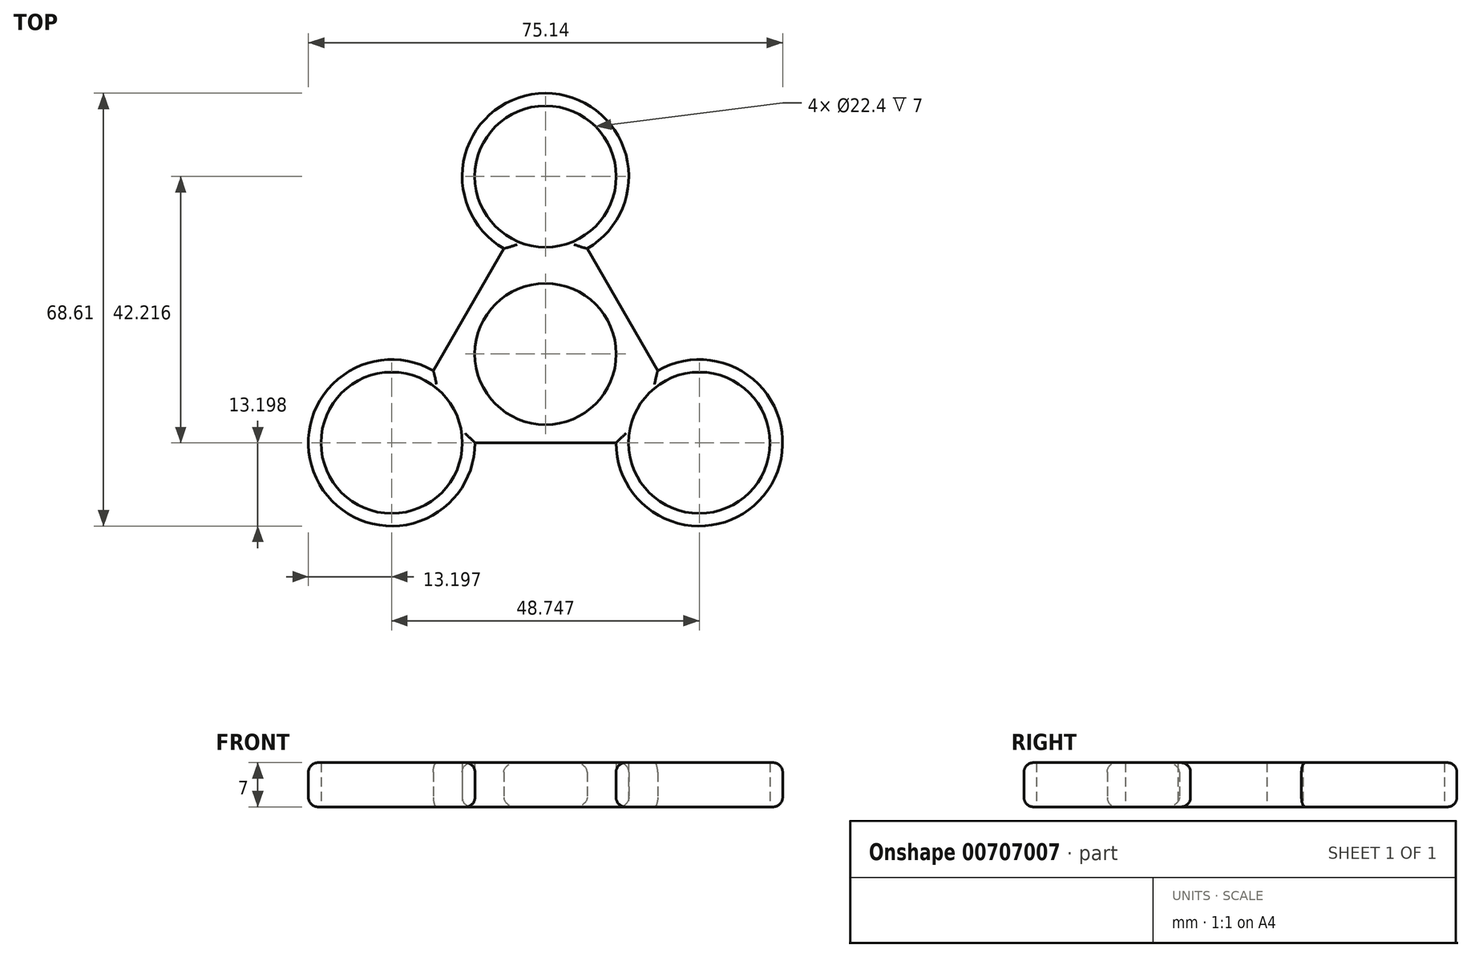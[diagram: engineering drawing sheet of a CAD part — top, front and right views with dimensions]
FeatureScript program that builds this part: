
annotation { "Feature Type Name" : "Feature", "Feature Type Description" : "" }
export const myFeature = defineFeature(function(context is Context, id is Id, definition is map)
    precondition{}
    {
        {
            var Q0;
            Q0=qCreatedBy(makeId("Top.planeOp"),FACE);
            var sketch = newSketch(context, id + "F0", { "sketchPlane" : qUnion([Q0])});
            skCircle(sketch, "E0", {"center": v(0, 0) * mm, "radius": 11.2 * mm});
            skCircle(sketch, "E1", {"center": v(0, 28.14) * mm, "radius": 11.2 * mm});
            skArc(sketch, "E2", {"start": v(6.6, 16.71) * mm, "mid": v(0, 41.34) * mm, "end": v(-6.6, 16.71) * mm});
            skArc(sketch, "E3.1.0", {"start": v(-17.77, -2.64) * mm, "mid": v(-35.8, -20.67) * mm, "end": v(-11.17, -14.07) * mm});
            skCircle(sketch, "E3.1.1", {"center": v(-24.37, -14.07) * mm, "radius": 11.2 * mm});
            skArc(sketch, "E3.2.0", {"start": v(11.17, -14.07) * mm, "mid": v(35.8, -20.67) * mm, "end": v(17.77, -2.64) * mm});
            skCircle(sketch, "E3.2.1", {"center": v(24.37, -14.07) * mm, "radius": 11.2 * mm});
            skLineSegment(sketch, "E4", {"start": v(-11.17, -14.07) * mm, "end": v(11.17, -14.07) * mm});
            skLineSegment(sketch, "E5.1.0", {"start": v(17.77, -2.64) * mm, "end": v(6.6, 16.71) * mm});
            skLineSegment(sketch, "E5.2.0", {"start": v(-6.6, 16.71) * mm, "end": v(-17.77, -2.64) * mm});
            skSolve(sketch);
        }
        {
            var Q0;
            Q0=makeQuery(id+"F0.imprint","IMPRINT",FACE,{"disambiguationData":[TD([[makeQuery(id+"F0.imprint","IMPRINT",EDGE,{"derivedFrom":sQuery(id+"F0.wireOp",EDGE,"E0")}),-1.0]])]});
            extrude(context, id + "F1", {"entities" : qUnion([Q0]), "depth" : 7 * mm, "offsetDistance" : 25 * mm});
        }
        {
            var Q0;
            Q0=makeQuery(id+"F1.opExtrude","CAP_EDGE",EDGE,{"disambiguationData":[OSD([sQuery(id+"F0.wireOp",EDGE,"E4")])],"isStart":false});
            var Q1;
            Q1=makeQuery(id+"F1.opExtrude","CAP_EDGE",EDGE,{"disambiguationData":[OSD([sQuery(id+"F0.wireOp",EDGE,"E4")])],"isStart":true});
            var Q2;
            Q2=makeQuery(id+"F1.opExtrude","CAP_EDGE",EDGE,{"disambiguationData":[OSD([sQuery(id+"F0.wireOp",EDGE,"E3.1.0")])],"isStart":false});
            var Q3;
            Q3=makeQuery(id+"F1.opExtrude","CAP_EDGE",EDGE,{"disambiguationData":[OSD([sQuery(id+"F0.wireOp",EDGE,"E5.2.0")])],"isStart":false});
            var Q4;
            Q4=makeQuery(id+"F1.opExtrude","CAP_EDGE",EDGE,{"disambiguationData":[OSD([sQuery(id+"F0.wireOp",EDGE,"E2")])],"isStart":false});
            var Q5;
            Q5=makeQuery(id+"F1.opExtrude","CAP_EDGE",EDGE,{"disambiguationData":[OSD([sQuery(id+"F0.wireOp",EDGE,"E5.1.0")])],"isStart":false});
            var Q6;
            Q6=makeQuery(id+"F1.opExtrude","CAP_EDGE",EDGE,{"disambiguationData":[OSD([sQuery(id+"F0.wireOp",EDGE,"E3.2.0")])],"isStart":false});
            fillet(context, id + "F2", {"entities" : qUnion([Q0, Q1, Q2, Q3, Q4, Q5, Q6]), "radius" : 1.5 * mm, "tangentPropagation" : true, "allowEdgeOverflow" : false});
        }
        {
            var Q0;
            Q0=makeQuery(id+"F1.opExtrude","CAP_EDGE",EDGE,{"disambiguationData":[OSD([sQuery(id+"F0.wireOp",EDGE,"E3.1.0")])],"isStart":true});
            var Q1;
            Q1=makeQuery(id+"F1.opExtrude","CAP_EDGE",EDGE,{"disambiguationData":[OSD([sQuery(id+"F0.wireOp",EDGE,"E5.2.0")])],"isStart":true});
            var Q2;
            Q2=makeQuery(id+"F1.opExtrude","CAP_EDGE",EDGE,{"disambiguationData":[OSD([sQuery(id+"F0.wireOp",EDGE,"E2")])],"isStart":true});
            var Q3;
            Q3=makeQuery(id+"F1.opExtrude","CAP_EDGE",EDGE,{"disambiguationData":[OSD([sQuery(id+"F0.wireOp",EDGE,"E5.1.0")])],"isStart":true});
            var Q4;
            Q4=makeQuery(id+"F1.opExtrude","CAP_EDGE",EDGE,{"disambiguationData":[OSD([sQuery(id+"F0.wireOp",EDGE,"E3.2.0")])],"isStart":true});
            fillet(context, id + "F3", {"entities" : qUnion([Q0, Q1, Q2, Q3, Q4]), "radius" : 1.5 * mm, "tangentPropagation" : true, "allowEdgeOverflow" : false});
        }
    });
